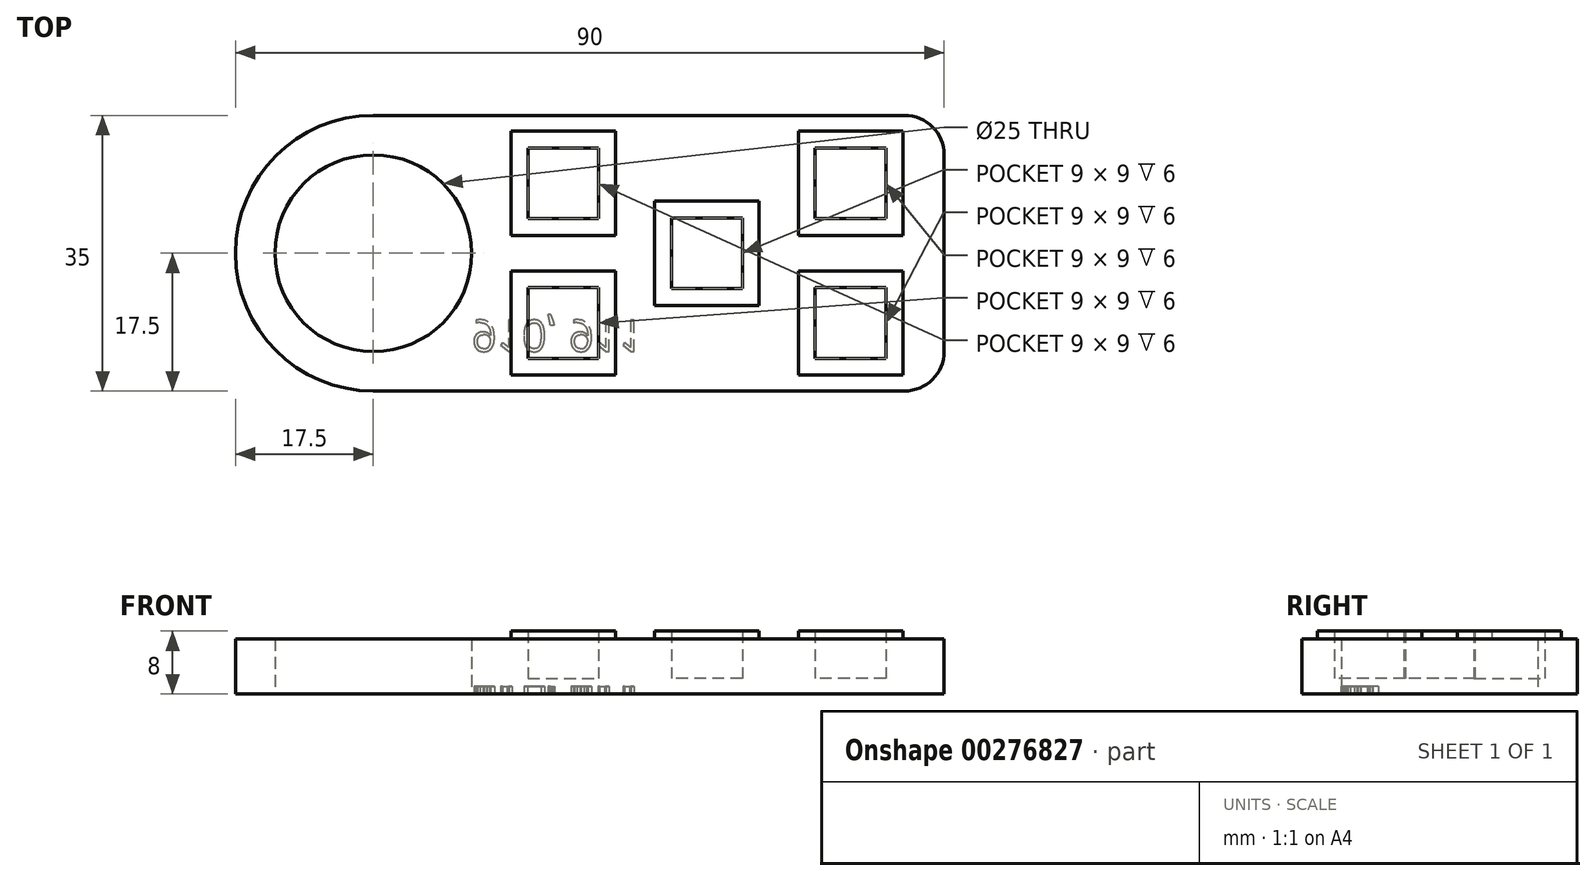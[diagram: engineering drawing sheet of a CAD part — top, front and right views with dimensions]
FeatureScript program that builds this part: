
annotation { "Feature Type Name" : "Feature", "Feature Type Description" : "" }
export const myFeature = defineFeature(function(context is Context, id is Id, definition is map)
    precondition{}
    {
        {
            var Q0;
            Q0=qCreatedBy(makeId("Top.planeOp"),FACE);
            var sketch = newSketch(context, id + "F0", { "sketchPlane" : qUnion([Q0])});
            skLineSegment(sketch, "E0.bottom", {"start": v(17.5, 0) * mm, "end": v(85, 0) * mm});
            skLineSegment(sketch, "E0.top", {"start": v(17.5, 35) * mm, "end": v(85, 35) * mm});
            skLineSegment(sketch, "E0.left", {"start": v(0, 17.5) * mm, "end": v(0, 17.5) * mm});
            skLineSegment(sketch, "E0.right", {"start": v(90, 5) * mm, "end": v(90, 30) * mm});
            skLineSegment(sketch, "E1.bottom", {"start": v(0, 0) * mm, "end": v(17.5, 0) * mm, "construction": true});
            skLineSegment(sketch, "E1.top", {"start": v(0, 17.5) * mm, "end": v(17.5, 17.5) * mm, "construction": true});
            skLineSegment(sketch, "E1.left", {"start": v(0, 0) * mm, "end": v(0, 17.5) * mm, "construction": true});
            skLineSegment(sketch, "E1.right", {"start": v(17.5, 0) * mm, "end": v(17.5, 17.5) * mm, "construction": true});
            skCircle(sketch, "E2", {"center": v(17.5, 17.5) * mm, "radius": 12.5 * mm});
            skPoint(sketch, "E3.visualSharp", {"position": v(0, 0) * mm});
            skArc(sketch, "E3.filletArc", {"start": v(0, 17.5) * mm, "mid": v(5.13, 5.13) * mm, "end": v(17.5, 0) * mm});
            skPoint(sketch, "E4.visualSharp", {"position": v(0, 35) * mm});
            skArc(sketch, "E4.filletArc", {"start": v(17.5, 35) * mm, "mid": v(5.13, 29.87) * mm, "end": v(0, 17.5) * mm});
            skPoint(sketch, "E5.visualSharp", {"position": v(90, 35) * mm});
            skArc(sketch, "E5.filletArc", {"start": v(90, 30) * mm, "mid": v(88.54, 33.54) * mm, "end": v(85, 35) * mm});
            skPoint(sketch, "E6.visualSharp", {"position": v(90, 0) * mm});
            skArc(sketch, "E6.filletArc", {"start": v(85, 0) * mm, "mid": v(88.54, 1.46) * mm, "end": v(90, 5) * mm});
            skSolve(sketch);
        }
        {
            var Q0;
            Q0=makeQuery(id+"F0.imprint","IMPRINT",FACE,{"disambiguationData":[TD([[makeQuery(id+"F0.imprint","IMPRINT",EDGE,{"derivedFrom":sQuery(id+"F0.wireOp",EDGE,"E0.bottom")}),1.0]])]});
            extrude(context, id + "F1", {"entities" : qUnion([Q0]), "depth" : 7 * mm});
        }
        {
            var Q0;
            Q0=makeQuery(id+"F1.opExtrude","CAP_FACE",FACE,{"disambiguationData":[OSD([sQuery(id+"F0.wireOp",EDGE,"E0.bottom"),sQuery(id+"F0.wireOp",EDGE,"E0.top"),sQuery(id+"F0.wireOp",EDGE,"E0.right"),sQuery(id+"F0.wireOp",EDGE,"E2"),sQuery(id+"F0.wireOp",EDGE,"E3.filletArc"),sQuery(id+"F0.wireOp",EDGE,"E4.filletArc"),sQuery(id+"F0.wireOp",EDGE,"E5.filletArc"),sQuery(id+"F0.wireOp",EDGE,"E6.filletArc")])],"isStart":false});
            var sketch = newSketch(context, id + "F2", { "sketchPlane" : qUnion([Q0])});
            skLineSegment(sketch, "E7.bottom", {"start": v(0, 0) * mm, "end": v(35, 0) * mm, "construction": true});
            skLineSegment(sketch, "E7.top", {"start": v(0, 33) * mm, "end": v(35, 33) * mm, "construction": true});
            skLineSegment(sketch, "E7.left", {"start": v(0, 0) * mm, "end": v(0, 33) * mm, "construction": true});
            skLineSegment(sketch, "E7.right", {"start": v(35, 0) * mm, "end": v(35, 33) * mm, "construction": true});
            skLineSegment(sketch, "E8.bottom", {"start": v(35, 33) * mm, "end": v(84.75, 33) * mm, "construction": true});
            skLineSegment(sketch, "E8.top", {"start": v(35, 2) * mm, "end": v(84.75, 2) * mm, "construction": true});
            skLineSegment(sketch, "E8.left", {"start": v(35, 33) * mm, "end": v(35, 2) * mm, "construction": true});
            skLineSegment(sketch, "E8.right", {"start": v(84.75, 33) * mm, "end": v(84.75, 2) * mm, "construction": true});
            skLineSegment(sketch, "E9", {"start": v(35, 33) * mm, "end": v(84.75, 2) * mm, "construction": true});
            skLineSegment(sketch, "E10.bottom", {"start": v(35, 33) * mm, "end": v(48.25, 33) * mm});
            skLineSegment(sketch, "E10.top", {"start": v(35, 19.75) * mm, "end": v(48.25, 19.75) * mm});
            skLineSegment(sketch, "E10.left", {"start": v(35, 33) * mm, "end": v(35, 19.75) * mm});
            skLineSegment(sketch, "E10.right", {"start": v(48.25, 33) * mm, "end": v(48.25, 19.75) * mm});
            skLineSegment(sketch, "E11.bottom", {"start": v(35, 2) * mm, "end": v(48.25, 2) * mm});
            skLineSegment(sketch, "E11.top", {"start": v(35, 15.25) * mm, "end": v(48.25, 15.25) * mm});
            skLineSegment(sketch, "E11.left", {"start": v(35, 2) * mm, "end": v(35, 15.25) * mm});
            skLineSegment(sketch, "E11.right", {"start": v(48.25, 2) * mm, "end": v(48.25, 15.25) * mm});
            skLineSegment(sketch, "E12.bottom", {"start": v(84.75, 33) * mm, "end": v(71.5, 33) * mm});
            skLineSegment(sketch, "E12.top", {"start": v(84.75, 19.75) * mm, "end": v(71.5, 19.75) * mm});
            skLineSegment(sketch, "E12.left", {"start": v(84.75, 33) * mm, "end": v(84.75, 19.75) * mm});
            skLineSegment(sketch, "E12.right", {"start": v(71.5, 33) * mm, "end": v(71.5, 19.75) * mm});
            skLineSegment(sketch, "E13.bottom", {"start": v(84.75, 2) * mm, "end": v(71.5, 2) * mm});
            skLineSegment(sketch, "E13.top", {"start": v(84.75, 15.25) * mm, "end": v(71.5, 15.25) * mm});
            skLineSegment(sketch, "E13.left", {"start": v(84.75, 2) * mm, "end": v(84.75, 15.25) * mm});
            skLineSegment(sketch, "E13.right", {"start": v(71.5, 2) * mm, "end": v(71.5, 15.25) * mm});
            skLineSegment(sketch, "E14.bottom", {"start": v(66.5, 24.13) * mm, "end": v(53.25, 24.13) * mm});
            skLineSegment(sketch, "E14.top", {"start": v(66.5, 10.88) * mm, "end": v(53.25, 10.88) * mm});
            skLineSegment(sketch, "E14.left", {"start": v(66.5, 24.13) * mm, "end": v(66.5, 10.88) * mm});
            skLineSegment(sketch, "E14.right", {"start": v(53.25, 24.13) * mm, "end": v(53.25, 10.88) * mm});
            skPoint(sketch, "E14.middle", {"position": v(59.88, 17.5) * mm});
            skLineSegment(sketch, "E15", {"start": v(48.25, 33) * mm, "end": v(35, 19.75) * mm, "construction": true});
            skLineSegment(sketch, "E16", {"start": v(48.25, 15.25) * mm, "end": v(35, 2) * mm, "construction": true});
            skLineSegment(sketch, "E17", {"start": v(84.75, 33) * mm, "end": v(71.5, 19.75) * mm, "construction": true});
            skLineSegment(sketch, "E18", {"start": v(84.75, 15.25) * mm, "end": v(71.5, 2) * mm, "construction": true});
            skLineSegment(sketch, "E19.bottom", {"start": v(37.13, 21.88) * mm, "end": v(46.13, 21.88) * mm});
            skLineSegment(sketch, "E19.top", {"start": v(37.13, 30.88) * mm, "end": v(46.13, 30.88) * mm});
            skLineSegment(sketch, "E19.left", {"start": v(37.13, 21.88) * mm, "end": v(37.13, 30.88) * mm});
            skLineSegment(sketch, "E19.right", {"start": v(46.13, 21.88) * mm, "end": v(46.13, 30.88) * mm});
            skPoint(sketch, "E19.middle", {"position": v(41.62, 26.38) * mm});
            skLineSegment(sketch, "E20.bottom", {"start": v(37.13, 13.13) * mm, "end": v(46.13, 13.13) * mm});
            skLineSegment(sketch, "E20.top", {"start": v(37.13, 4.12) * mm, "end": v(46.13, 4.12) * mm});
            skLineSegment(sketch, "E20.left", {"start": v(37.13, 13.13) * mm, "end": v(37.13, 4.13) * mm});
            skLineSegment(sketch, "E20.right", {"start": v(46.13, 13.13) * mm, "end": v(46.13, 4.13) * mm});
            skPoint(sketch, "E20.middle", {"position": v(41.62, 8.62) * mm});
            skLineSegment(sketch, "E21.bottom", {"start": v(73.62, 13.12) * mm, "end": v(82.62, 13.12) * mm});
            skLineSegment(sketch, "E21.top", {"start": v(73.62, 4.12) * mm, "end": v(82.62, 4.12) * mm});
            skLineSegment(sketch, "E21.left", {"start": v(73.62, 13.12) * mm, "end": v(73.62, 4.12) * mm});
            skLineSegment(sketch, "E21.right", {"start": v(82.62, 13.12) * mm, "end": v(82.62, 4.12) * mm});
            skPoint(sketch, "E21.middle", {"position": v(78.12, 8.62) * mm});
            skLineSegment(sketch, "E22.bottom", {"start": v(82.63, 21.88) * mm, "end": v(73.63, 21.88) * mm});
            skLineSegment(sketch, "E22.top", {"start": v(82.63, 30.88) * mm, "end": v(73.63, 30.88) * mm});
            skLineSegment(sketch, "E22.left", {"start": v(82.63, 21.88) * mm, "end": v(82.63, 30.88) * mm});
            skLineSegment(sketch, "E22.right", {"start": v(73.63, 21.88) * mm, "end": v(73.63, 30.88) * mm});
            skPoint(sketch, "E22.middle", {"position": v(78.12, 26.38) * mm});
            skLineSegment(sketch, "E23.bottom", {"start": v(64.38, 22) * mm, "end": v(55.38, 22) * mm});
            skLineSegment(sketch, "E23.top", {"start": v(64.38, 13) * mm, "end": v(55.38, 13) * mm});
            skLineSegment(sketch, "E23.left", {"start": v(64.38, 22) * mm, "end": v(64.38, 13) * mm});
            skLineSegment(sketch, "E23.right", {"start": v(55.38, 22) * mm, "end": v(55.38, 13) * mm});
            skSolve(sketch);
        }
        {
            var Q0;
            Q0=makeQuery(id+"F2.imprint","IMPRINT",FACE,{"disambiguationData":[TD([[makeQuery(id+"F2.imprint","IMPRINT",EDGE,{"derivedFrom":sQuery(id+"F2.wireOp",EDGE,"E10.bottom")}),-1.0]])]});
            var Q1;
            Q1=makeQuery(id+"F2.imprint","IMPRINT",FACE,{"disambiguationData":[TD([[makeQuery(id+"F2.imprint","IMPRINT",EDGE,{"derivedFrom":sQuery(id+"F2.wireOp",EDGE,"E11.bottom")}),1.0]])]});
            var Q2;
            Q2=makeQuery(id+"F2.imprint","IMPRINT",FACE,{"disambiguationData":[TD([[makeQuery(id+"F2.imprint","IMPRINT",EDGE,{"derivedFrom":sQuery(id+"F2.wireOp",EDGE,"E14.bottom")}),1.0]])]});
            var Q3;
            Q3=makeQuery(id+"F2.imprint","IMPRINT",FACE,{"disambiguationData":[TD([[makeQuery(id+"F2.imprint","IMPRINT",EDGE,{"derivedFrom":sQuery(id+"F2.wireOp",EDGE,"E13.bottom")}),-1.0]])]});
            var Q4;
            Q4=makeQuery(id+"F2.imprint","IMPRINT",FACE,{"disambiguationData":[TD([[makeQuery(id+"F2.imprint","IMPRINT",EDGE,{"derivedFrom":sQuery(id+"F2.wireOp",EDGE,"E12.bottom")}),1.0]])]});
            extrude(context, id + "F3", {"entities" : qUnion([Q0, Q1, Q2, Q3, Q4]), "operationType" : NewBodyOperationType.ADD, "depth" : 1 * mm});
        }
        {
            var Q0;
            Q0=makeQuery(id+"F2.imprint","IMPRINT",FACE,{"disambiguationData":[TD([[makeQuery(id+"F2.imprint","IMPRINT",EDGE,{"derivedFrom":sQuery(id+"F2.wireOp",EDGE,"E19.bottom")}),1.0]])]});
            var Q1;
            Q1=makeQuery(id+"F2.imprint","IMPRINT",FACE,{"disambiguationData":[TD([[makeQuery(id+"F2.imprint","IMPRINT",EDGE,{"derivedFrom":sQuery(id+"F2.wireOp",EDGE,"E20.bottom")}),-1.0]])]});
            var Q2;
            Q2=makeQuery(id+"F2.imprint","IMPRINT",FACE,{"disambiguationData":[TD([[makeQuery(id+"F2.imprint","IMPRINT",EDGE,{"derivedFrom":sQuery(id+"F2.wireOp",EDGE,"E23.bottom")}),1.0]])]});
            var Q3;
            Q3=makeQuery(id+"F2.imprint","IMPRINT",FACE,{"disambiguationData":[TD([[makeQuery(id+"F2.imprint","IMPRINT",EDGE,{"derivedFrom":sQuery(id+"F2.wireOp",EDGE,"E22.bottom")}),-1.0]])]});
            var Q4;
            Q4=makeQuery(id+"F2.imprint","IMPRINT",FACE,{"disambiguationData":[TD([[makeQuery(id+"F2.imprint","IMPRINT",EDGE,{"derivedFrom":sQuery(id+"F2.wireOp",EDGE,"E21.bottom")}),-1.0]])]});
            extrude(context, id + "F4", {"entities" : qUnion([Q0, Q1, Q2, Q3, Q4]), "operationType" : NewBodyOperationType.REMOVE, "oppositeDirection" : true, "depth" : 5 * mm});
        }
        {
            var Q0;
            Q0=makeQuery(id+"F1.opExtrude","CAP_FACE",FACE,{"disambiguationData":[OSD([sQuery(id+"F0.wireOp",EDGE,"E0.bottom"),sQuery(id+"F0.wireOp",EDGE,"E0.top"),sQuery(id+"F0.wireOp",EDGE,"E0.right"),sQuery(id+"F0.wireOp",EDGE,"E2"),sQuery(id+"F0.wireOp",EDGE,"E3.filletArc"),sQuery(id+"F0.wireOp",EDGE,"E4.filletArc"),sQuery(id+"F0.wireOp",EDGE,"E5.filletArc"),sQuery(id+"F0.wireOp",EDGE,"E6.filletArc")])],"isStart":true});
            var sketch = newSketch(context, id + "F5", { "sketchPlane" : qUnion([Q0])});
            skLineSegment(sketch, "E24.bottom", {"start": v(0, 0) * mm, "end": v(30, 0) * mm, "construction": true});
            skLineSegment(sketch, "E24.top", {"start": v(0, -5) * mm, "end": v(30, -5) * mm, "construction": true});
            skLineSegment(sketch, "E24.left", {"start": v(0, 0) * mm, "end": v(0, -5) * mm, "construction": true});
            skLineSegment(sketch, "E24.right", {"start": v(30, 0) * mm, "end": v(30, -5) * mm, "construction": true});
            skText(sketch, "E25", { "text": "910, 911", "fontName": "OpenSans-Regular.ttf"});
            const initialGuessF5  = {"E25": [0.03, -0.009, 1, 0, 0.004]};
            skSetInitialGuess(sketch, initialGuessF5);
            skSolve(sketch);
        }
        {
            var Q0;
            Q0 = qSketchRegion(id + "F5", true);
            extrude(context, id + "F6", {"entities" : qUnion([Q0]), "operationType" : NewBodyOperationType.REMOVE, "oppositeDirection" : true, "depth" : 1 * mm});
        }
    });
